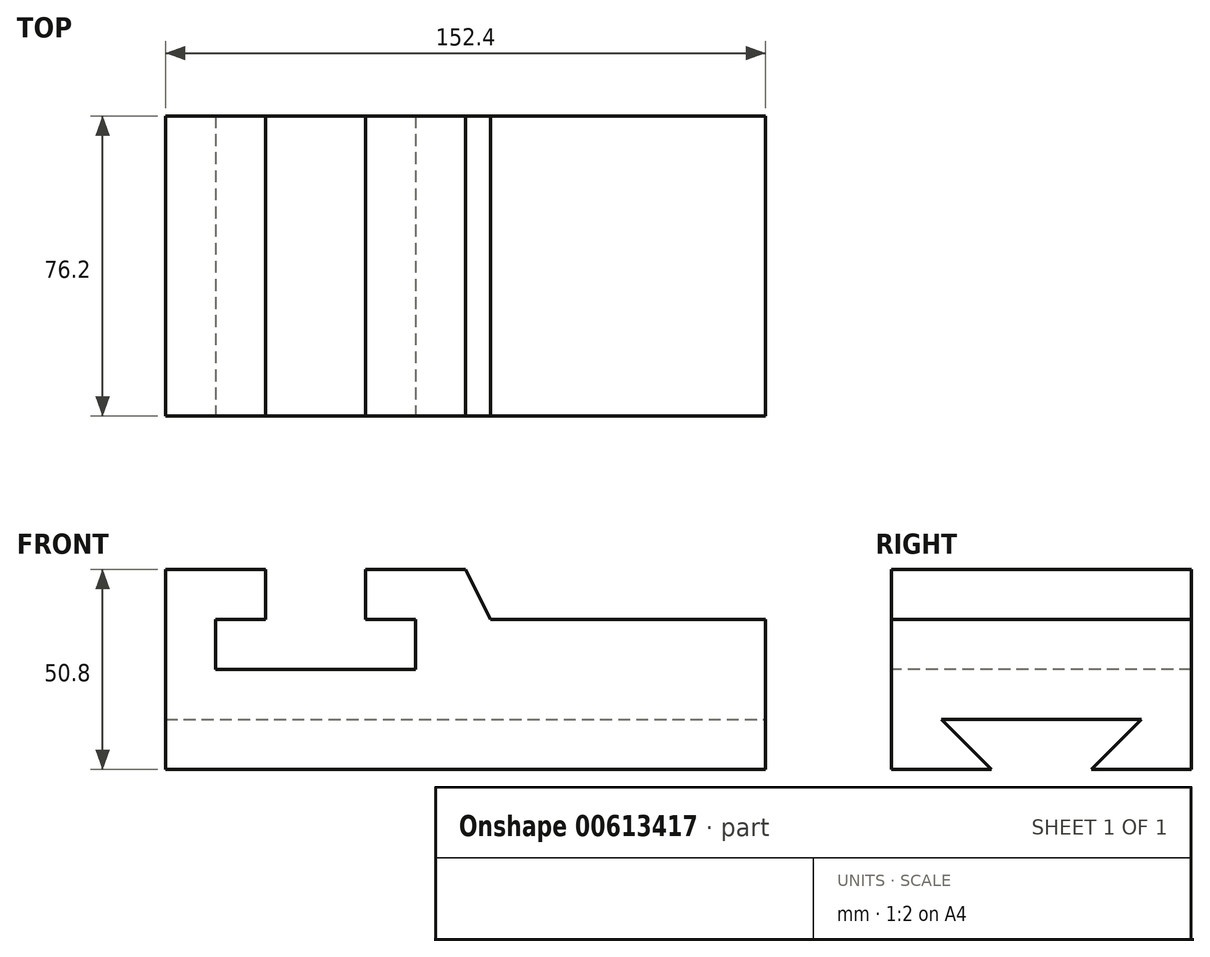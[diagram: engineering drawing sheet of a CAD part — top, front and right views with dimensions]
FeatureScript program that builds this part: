
annotation { "Feature Type Name" : "Feature", "Feature Type Description" : "" }
export const myFeature = defineFeature(function(context is Context, id is Id, definition is map)
    precondition{}
    {
        {
            var Q0;
            Q0=qCreatedBy(makeId("Front.planeOp"),FACE);
            var sketch = newSketch(context, id + "F0", { "sketchPlane" : qUnion([Q0])});
            skLineSegment(sketch, "E0", {"start": v(0, 0) * mm, "end": v(0, 50.8) * mm});
            skLineSegment(sketch, "E1", {"start": v(0, 50.8) * mm, "end": v(25.4, 50.8) * mm});
            skLineSegment(sketch, "E2", {"start": v(25.4, 50.8) * mm, "end": v(25.4, 38.1) * mm});
            skLineSegment(sketch, "E3", {"start": v(25.4, 38.1) * mm, "end": v(12.7, 38.1) * mm});
            skLineSegment(sketch, "E4", {"start": v(12.7, 38.1) * mm, "end": v(12.7, 25.4) * mm});
            skLineSegment(sketch, "E5", {"start": v(12.7, 25.4) * mm, "end": v(63.5, 25.4) * mm});
            skLineSegment(sketch, "E6", {"start": v(50.8, 38.1) * mm, "end": v(50.8, 38.1) * mm});
            skLineSegment(sketch, "E7", {"start": v(50.8, 38.1) * mm, "end": v(50.8, 50.8) * mm});
            skLineSegment(sketch, "E8", {"start": v(50.8, 50.8) * mm, "end": v(76.2, 50.8) * mm});
            skLineSegment(sketch, "E9", {"start": v(152.4, 38.1) * mm, "end": v(152.4, 0) * mm});
            skLineSegment(sketch, "E10", {"start": v(152.4, 0) * mm, "end": v(0, 0) * mm});
            skLineSegment(sketch, "E11", {"start": v(50.8, 38.1) * mm, "end": v(63.5, 38.1) * mm});
            skLineSegment(sketch, "E12", {"start": v(63.5, 38.1) * mm, "end": v(63.5, 25.4) * mm});
            skLineSegment(sketch, "E13", {"start": v(82.55, 38.1) * mm, "end": v(76.2, 50.8) * mm});
            skLineSegment(sketch, "E14", {"start": v(82.55, 38.1) * mm, "end": v(152.4, 38.1) * mm});
            skSolve(sketch);
        }
        {
            var Q0;
            Q0 = qSketchRegion(id + "F0", true);
            extrude(context, id + "F1", {"entities" : qUnion([Q0]), "oppositeDirection" : true, "depth" : 76.2 * mm, "offsetDistance" : 25.4 * mm});
        }
        {
            var Q0;
            Q0=makeQuery(id+"F1.opExtrude","SWEPT_FACE",FACE,{"disambiguationData":[OSD([sQuery(id+"F0.wireOp",EDGE,"E9")])]});
            var sketch = newSketch(context, id + "F2", { "sketchPlane" : qUnion([Q0])});
            skLineSegment(sketch, "E15", {"start": v(12.7, 12.7) * mm, "end": v(25.4, 0) * mm});
            skLineSegment(sketch, "E16", {"start": v(12.7, 12.7) * mm, "end": v(63.5, 12.7) * mm});
            skLineSegment(sketch, "E17", {"start": v(63.5, 12.7) * mm, "end": v(50.8, 0) * mm});
            skLineSegment(sketch, "E18", {"start": v(25.4, 0) * mm, "end": v(50.8, 0) * mm});
            skSolve(sketch);
        }
        {
            var Q0;
            Q0=makeQuery(id+"F2.imprint","IMPRINT",FACE,{"disambiguationData":[TD([[makeQuery(id+"F2.imprint","IMPRINT",EDGE,{"derivedFrom":sQuery(id+"F2.wireOp",EDGE,"E15")}),1.0]])]});
            extrude(context, id + "F3", {"entities" : qUnion([Q0]), "operationType" : NewBodyOperationType.REMOVE, "oppositeDirection" : true, "depth" : 152.4 * mm, "offsetDistance" : 25.4 * mm});
        }
    });
